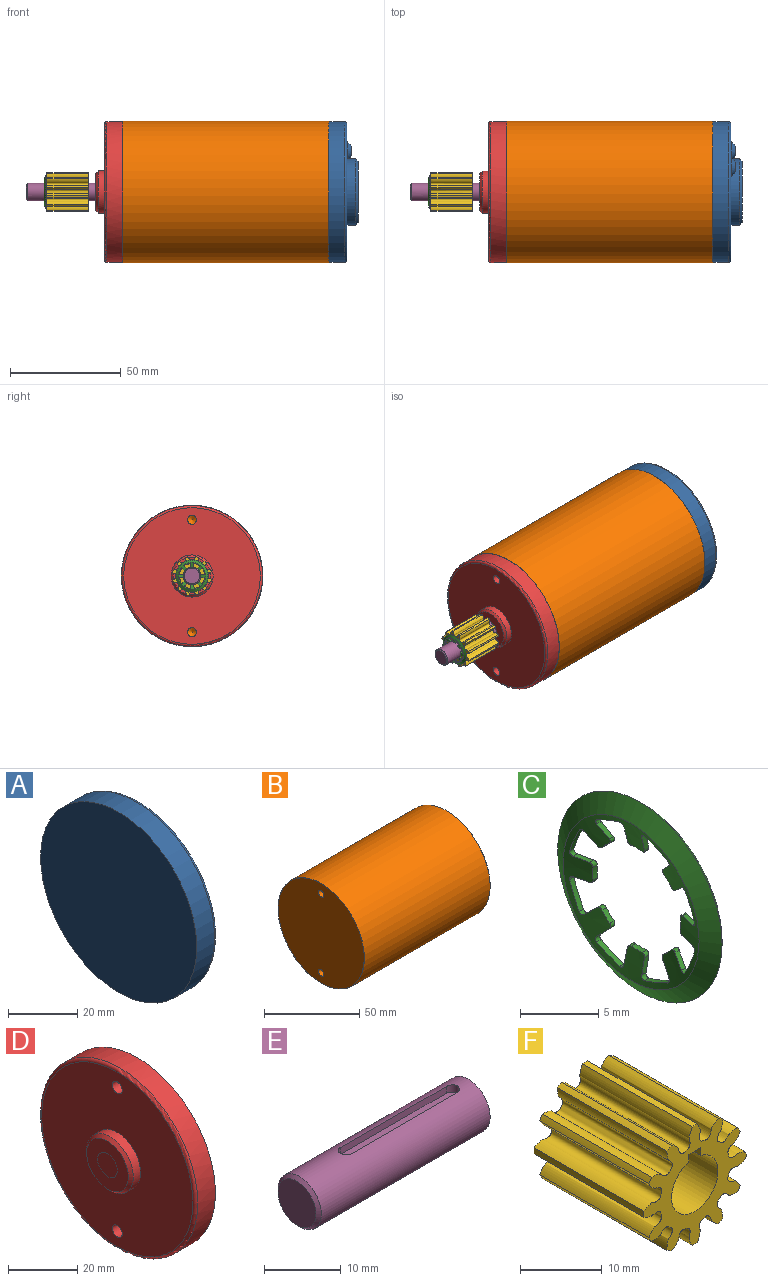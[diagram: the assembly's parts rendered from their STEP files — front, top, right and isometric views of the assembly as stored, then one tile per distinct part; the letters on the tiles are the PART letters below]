
ASSEMBLY  parts=6 mates=5
PART A: 13 faces, bbox 13.2x69x69 mm
  f0: plane 4.24x4.24mm, normal (1,0,0), area 14.1mm2, adj f3
  f1: plane 28.04x28.04mm, normal (1,0,0), area 617.6mm2, adj f4
  f2: plane 4.24x4.24mm, normal (1,0,0), area 14.1mm2, adj f5
  f3: cone r=2.12mm half-angle=45deg, axis (-1,0,0), area 62.9mm2, adj f0,f6
  f4: cone r=14.02mm half-angle=45deg, axis (-1,0,0), area 131.2mm2, adj f1,f7
  f5: cone r=2.12mm half-angle=45deg, axis (-1,0,0), area 62.9mm2, adj f2,f8
  f6: cylinder r=4.32mm len=8.64mm, axis (-1,0,0), area 1.3mm2, adj f3,f9
  f7: cylinder r=15.04mm len=30.07mm, axis (1,0,0), area 376.4mm2, adj f4,f9
  f8: cylinder r=4.32mm len=8.64mm, axis (-1,0,0), area 1.3mm2, adj f5,f9
  f9: plane 61.75x61.75mm, normal (1,0,0), area 2167.7mm2, adj f6,f7,f8,f10
  f10: torus R=30.88mm, axis (1,0,0), area 311mm2, adj f9,f11
  f11: cylinder r=31.88mm len=63.75mm, axis (1,0,0), area 1448mm2, adj f10,f12
  f12: plane 63.75x63.75mm, normal (-1,0,0), area 3192.3mm2, adj f11
PART B: 9 faces, bbox 93.1x64x64 mm
  f0: plane 63.75x63.75mm, normal (1,0,0), area 3192.3mm2, adj f1
  f1: plane 64.01x64.01mm, normal (1,0,0), area 25.5mm2, adj f0,f2
  f2: cylinder r=32mm len=93.14mm, axis (1,0,0), area 18729.4mm2, adj f1,f3
  f3: plane 64.01x64.01mm, normal (-1,0,0), area 25.5mm2, adj f2,f4
  f4: plane 63.75x63.75mm, normal (-1,0,0), area 3166.7mm2, adj f3,f6,f8
  f5: cone r=2.02mm half-angle=59deg, axis (-1,0,0), area 14.9mm2, adj f6
  f6: cylinder r=2.02mm len=5.38mm, axis (-1,0,0), area 68.3mm2, adj f4,f5
  f7: cone r=2.02mm half-angle=59deg, axis (-1,0,0), area 14.9mm2, adj f8
  f8: cylinder r=2.02mm len=5.38mm, axis (-1,0,0), area 68.3mm2, adj f4,f7
PART C: 69 faces, bbox 1.1x14.9x14.9 mm
  f0: cylinder r=0.25mm len=0.46mm, axis (-1,0,0), area 0.2mm2, adj f11,f12,f14,f63
  f1: cylinder r=0.25mm len=0.46mm, axis (-1,0,0), area 0.2mm2, adj f11,f12,f56,f62
  f2: cylinder r=0.25mm len=0.46mm, axis (-1,0,0), area 0.2mm2, adj f11,f12,f49,f55
  f3: cylinder r=0.25mm len=0.46mm, axis (-1,0,0), area 0.2mm2, adj f11,f12,f42,f48
  f4: cylinder r=0.25mm len=0.46mm, axis (-1,0,0), area 0.2mm2, adj f11,f12,f35,f41
  f5: cylinder r=0.25mm len=0.46mm, axis (-1,0,0), area 0.2mm2, adj f11,f12,f28,f34
  f6: cylinder r=0.25mm len=0.46mm, axis (-1,0,0), area 0.2mm2, adj f11,f12,f21,f27
  f7: cylinder r=0.25mm len=0.46mm, axis (-1,0,0), area 0.2mm2, adj f11,f12,f13,f17
  f8: cone r=7.42mm half-angle=58.1deg, axis (1,0,0), area 64.3mm2, adj f9,f12
  f9: cone r=7.15mm half-angle=45deg, axis (-1,0,0), area 17.4mm2, adj f8,f10
  f10: cone r=6.08mm half-angle=58.1deg, axis (1,0,0), area 52.2mm2, adj f9,f11
  f11: cone r=4.66mm half-angle=76.9deg, axis (-1,0,0), area 36.8mm2, adj f0,f1,f2,f3,f4,f5,f6,f7
  f12: cone r=4.66mm half-angle=76.9deg, axis (-1,0,0), area 38.9mm2, adj f0,f1,f2,f3,f4,f5,f6,f7
  f13: cylinder r=3.97mm len=0.99mm, axis (-1,0,0), area 0.4mm2, adj f7,f11,f12,f26
  f14: cylinder r=3.97mm len=0.7mm, axis (-1,0,0), area 0.4mm2, adj f0,f11,f12,f20
  f15: plane 0.89x0.86mm, normal (0,0.69,0.72), area 0.5mm2, adj f11,f12,f18,f20
  f16: cylinder r=11.39mm len=2.06mm, axis (-1,0,0), area 0.9mm2, adj f11,f12,f18,f19
  f17: plane 1.23x0.69mm, normal (0,-0.02,-1), area 0.5mm2, adj f7,f11,f12,f19
  f18: cylinder r=0.25mm len=0.46mm, axis (-1,0,0), area 0.2mm2, adj f11,f12,f15,f16
  f19: cylinder r=0.25mm len=0.46mm, axis (-1,0,0), area 0.2mm2, adj f11,f12,f16,f17
  f20: cylinder r=0.25mm len=0.46mm, axis (-1,0,0), area 0.2mm2, adj f11,f12,f14,f15
  f21: plane 0.89x0.86mm, normal (0,0.69,-0.72), area 0.5mm2, adj f6,f11,f12,f22
  f22: cylinder r=0.25mm len=0.46mm, axis (-1,0,0), area 0.2mm2, adj f11,f12,f21,f23
  f23: cylinder r=11.39mm len=2.06mm, axis (-1,0,0), area 0.9mm2, adj f11,f12,f22,f24
  f24: cylinder r=0.25mm len=0.46mm, axis (-1,0,0), area 0.2mm2, adj f11,f12,f23,f25
  f25: plane 1.23x0.69mm, normal (0,-0.02,1), area 0.5mm2, adj f11,f12,f24,f26
  f26: cylinder r=0.25mm len=0.46mm, axis (-1,0,0), area 0.2mm2, adj f11,f12,f13,f25
  f27: cylinder r=3.97mm len=0.7mm, axis (-1,0,0), area 0.4mm2, adj f6,f11,f12,f33
  f28: plane 1.23x0.69mm, normal (0,1,-0.02), area 0.5mm2, adj f5,f11,f12,f29
  f29: cylinder r=0.25mm len=0.46mm, axis (-1,0,0), area 0.2mm2, adj f11,f12,f28,f30
  f30: cylinder r=11.39mm len=2.06mm, axis (-1,0,0), area 0.9mm2, adj f11,f12,f29,f31
  f31: cylinder r=0.25mm len=0.46mm, axis (-1,0,0), area 0.2mm2, adj f11,f12,f30,f32
  f32: plane 0.89x0.86mm, normal (0,-0.72,0.69), area 0.5mm2, adj f11,f12,f31,f33
  f33: cylinder r=0.25mm len=0.46mm, axis (-1,0,0), area 0.2mm2, adj f11,f12,f27,f32
  f34: cylinder r=3.97mm len=0.99mm, axis (-1,0,0), area 0.4mm2, adj f5,f11,f12,f40
  f35: plane 0.89x0.86mm, normal (0,0.72,0.69), area 0.5mm2, adj f4,f11,f12,f36
  f36: cylinder r=0.25mm len=0.46mm, axis (-1,0,0), area 0.2mm2, adj f11,f12,f35,f37
  f37: cylinder r=11.39mm len=2.06mm, axis (-1,0,0), area 0.9mm2, adj f11,f12,f36,f38
  f38: cylinder r=0.25mm len=0.46mm, axis (-1,0,0), area 0.2mm2, adj f11,f12,f37,f39
  f39: plane 1.23x0.69mm, normal (0,-1,-0.02), area 0.5mm2, adj f11,f12,f38,f40
  f40: cylinder r=0.25mm len=0.46mm, axis (-1,0,0), area 0.2mm2, adj f11,f12,f34,f39
  f41: cylinder r=3.97mm len=0.7mm, axis (-1,0,0), area 0.4mm2, adj f4,f11,f12,f47
  f42: plane 1.23x0.69mm, normal (0,0.02,1), area 0.5mm2, adj f3,f11,f12,f43
  f43: cylinder r=0.25mm len=0.46mm, axis (-1,0,0), area 0.2mm2, adj f11,f12,f42,f44
  f44: cylinder r=11.39mm len=2.06mm, axis (-1,0,0), area 0.9mm2, adj f11,f12,f43,f45
  f45: cylinder r=0.25mm len=0.46mm, axis (-1,0,0), area 0.2mm2, adj f11,f12,f44,f46
  f46: plane 0.89x0.86mm, normal (0,-0.69,-0.72), area 0.5mm2, adj f11,f12,f45,f47
  f47: cylinder r=0.25mm len=0.46mm, axis (-1,0,0), area 0.2mm2, adj f11,f12,f41,f46
  f48: cylinder r=3.97mm len=0.99mm, axis (-1,0,0), area 0.4mm2, adj f3,f11,f12,f54
  f49: plane 0.89x0.86mm, normal (0,-0.69,0.72), area 0.5mm2, adj f2,f11,f12,f50
  f50: cylinder r=0.25mm len=0.46mm, axis (-1,0,0), area 0.2mm2, adj f11,f12,f49,f51
  f51: cylinder r=11.39mm len=2.06mm, axis (-1,0,0), area 0.9mm2, adj f11,f12,f50,f52
  f52: cylinder r=0.25mm len=0.46mm, axis (-1,0,0), area 0.2mm2, adj f11,f12,f51,f53
  f53: plane 1.23x0.69mm, normal (0,0.02,-1), area 0.5mm2, adj f11,f12,f52,f54
  f54: cylinder r=0.25mm len=0.46mm, axis (-1,0,0), area 0.2mm2, adj f11,f12,f48,f53
  f55: cylinder r=3.97mm len=0.7mm, axis (-1,0,0), area 0.4mm2, adj f2,f11,f12,f61
  f56: plane 1.23x0.69mm, normal (0,-1,0.02), area 0.5mm2, adj f1,f11,f12,f57
  f57: cylinder r=0.25mm len=0.46mm, axis (-1,0,0), area 0.2mm2, adj f11,f12,f56,f58
  f58: cylinder r=11.39mm len=2.06mm, axis (-1,0,0), area 0.9mm2, adj f11,f12,f57,f59
  f59: cylinder r=0.25mm len=0.46mm, axis (-1,0,0), area 0.2mm2, adj f11,f12,f58,f60
  f60: plane 0.89x0.86mm, normal (0,0.72,-0.69), area 0.5mm2, adj f11,f12,f59,f61
  f61: cylinder r=0.25mm len=0.46mm, axis (-1,0,0), area 0.2mm2, adj f11,f12,f55,f60
  f62: cylinder r=3.97mm len=0.99mm, axis (-1,0,0), area 0.4mm2, adj f1,f11,f12,f68
  f63: plane 0.89x0.86mm, normal (0,-0.72,-0.69), area 0.5mm2, adj f0,f11,f12,f64
  f64: cylinder r=0.25mm len=0.46mm, axis (-1,0,0), area 0.2mm2, adj f11,f12,f63,f65
  f65: cylinder r=11.39mm len=2.06mm, axis (-1,0,0), area 0.9mm2, adj f11,f12,f64,f66
  f66: cylinder r=0.25mm len=0.46mm, axis (-1,0,0), area 0.2mm2, adj f11,f12,f65,f67
  f67: plane 1.23x0.69mm, normal (0,1,0.02), area 0.5mm2, adj f11,f12,f66,f68
  f68: cylinder r=0.25mm len=0.46mm, axis (-1,0,0), area 0.2mm2, adj f11,f12,f62,f67
PART D: 10 faces, bbox 12.2x69x69 mm
  f0: cone r=9.53mm half-angle=45deg, axis (1,0,0), area 81.4mm2, adj f4,f7
  f1: cylinder r=2.02mm len=8.23mm, axis (-1,0,0), area 104.4mm2, adj f6,f9
  f2: cylinder r=2.02mm len=8.23mm, axis (-1,0,0), area 104.4mm2, adj f6,f9
  f3: torus R=30.88mm, axis (-1,0,0), area 311mm2, adj f5,f6
  f4: cylinder r=9.53mm len=19.05mm, axis (1,0,0), area 178.6mm2, adj f0,f6
  f5: cylinder r=31.88mm len=63.75mm, axis (1,0,0), area 1448mm2, adj f3,f9
  f6: plane 61.75x61.75mm, normal (-1,0,0), area 2684.5mm2, adj f1,f2,f3,f4
  f7: plane 17.02x17.02mm, normal (-1,0,0), area 177.2mm2, adj f0,f8
  f8: plane 8x8mm, normal (-1,0,0), area 50.3mm2, adj f7
  f9: plane 63.75x63.75mm, normal (1,0,0), area 3166.7mm2, adj f1,f2,f5
PART E: 9 faces, bbox 31.6x8x8 mm
  f0: plane 21.5x2mm, normal (0,0,1), area 42.1mm2, adj f2,f3,f4,f5
  f1: plane 7x7mm, normal (-1,0,0), area 38.5mm2, adj f6
  f2: plane 19.5x1.07mm, normal (0,1,0), area 20.9mm2, adj f0,f3,f5,f7
  f3: cylinder r=1mm len=2mm, axis (0,0,1), area 3.4mm2, adj f0,f2,f4,f7
  f4: plane 19.5x1.07mm, normal (0,-1,0), area 20.9mm2, adj f0,f3,f5,f7
  f5: cylinder r=1mm len=2mm, axis (0,0,-1), area 3.4mm2, adj f0,f2,f4,f7
  f6: cone r=4mm half-angle=45deg, axis (1,0,0), area 16.7mm2, adj f1,f7
  f7: cylinder r=4mm len=31.1mm, axis (1,0,0), area 739mm2, adj f2,f3,f4,f5,f6,f8
  f8: plane 8x8mm, normal (1,0,0), area 50.3mm2, adj f7
PART F: 30 faces, bbox 18x19.2x18 mm
  f0: cylinder r=4.03mm len=19mm, axis (0,1,0), area 441.1mm2, adj f2,f26,f27,f28
  f1: cylinder r=8.89mm len=19mm, axis (0,-1,0), area 17.2mm2, adj f2,f14,f15,f26
  f2: plane 17.95x17.95mm, normal (0,-1,0), area 120.6mm2, adj f0,f1,f3,f4,f5,f6,f7,f8
  f3: cylinder r=8.89mm len=19mm, axis (0,-1,0), area 17.2mm2, adj f2,f24,f25,f26
  f4: cylinder r=8.89mm len=19mm, axis (0,-1,0), area 17.2mm2, adj f2,f14,f25,f26
  f5: cylinder r=8.89mm len=19mm, axis (0,-1,0), area 17.2mm2, adj f2,f23,f24,f26
  f6: cylinder r=8.89mm len=19mm, axis (0,-1,0), area 17.2mm2, adj f2,f22,f23,f26
  f7: cylinder r=8.89mm len=19mm, axis (0,-1,0), area 17.2mm2, adj f2,f21,f22,f26
  f8: cylinder r=8.89mm len=19mm, axis (0,-1,0), area 17.2mm2, adj f2,f20,f21,f26
  f9: cylinder r=8.89mm len=19mm, axis (0,-1,0), area 17.2mm2, adj f2,f19,f20,f26
  f10: cylinder r=8.89mm len=19mm, axis (0,-1,0), area 17.2mm2, adj f2,f18,f19,f26
  f11: cylinder r=8.89mm len=19mm, axis (0,-1,0), area 17.2mm2, adj f2,f17,f18,f26
  f12: cylinder r=8.89mm len=19mm, axis (0,-1,0), area 17.2mm2, adj f2,f16,f17,f26
  f13: cylinder r=8.89mm len=19mm, axis (0,-1,0), area 17.2mm2, adj f2,f15,f16,f26
  f14: bspline ~19x3.59mm, area 136.3mm2, adj f1,f2,f4,f26
  f15: bspline ~19x3.59mm, area 136.3mm2, adj f1,f2,f13,f26
  f16: bspline ~19x3.56mm, area 136.3mm2, adj f2,f12,f13,f26
  f17: bspline ~19x3.59mm, area 136.3mm2, adj f2,f11,f12,f26
  f18: bspline ~19x3.59mm, area 136.3mm2, adj f2,f10,f11,f26
  f19: bspline ~19x3.56mm, area 136.3mm2, adj f2,f9,f10,f26
  f20: bspline ~19x3.59mm, area 136.3mm2, adj f2,f8,f9,f26
  f21: bspline ~19x3.59mm, area 136.3mm2, adj f2,f7,f8,f26
  f22: bspline ~19x3.56mm, area 136.3mm2, adj f2,f6,f7,f26
  f23: bspline ~19x3.59mm, area 136.3mm2, adj f2,f5,f6,f26
  f24: bspline ~19x3.59mm, area 136.3mm2, adj f2,f3,f5,f26
  f25: bspline ~19x3.56mm, area 136.3mm2, adj f2,f3,f4,f26
  f26: plane 17.95x17.95mm, normal (0,1,0), area 118.5mm2, adj f0,f1,f3,f4,f5,f6,f7,f8
  f27: plane 19x1.13mm, normal (1,0,0), area 21.5mm2, adj f0,f2,f26,f29
  f28: plane 19x1.13mm, normal (-1,0,0), area 21.5mm2, adj f0,f2,f26,f29
  f29: plane 19x2.05mm, normal (0,0,-1), area 39mm2, adj f2,f26,f27,f28
PLACE A t=(-54.8,0,0)mm
PLACE B t=(-54.8,0,0)mm
PLACE C rot(axis=(1,0,0),179.1deg) t=(-82.25,0,0)mm
PLACE D t=(-54.8,0,0)mm
PLACE E rot(axis=(-1,0,0),135.9deg) t=(-54.8,0,0)mm
PLACE F rot(axis=(-0.68,-0.68,-0.28),149.2deg) t=(-71.47,0,0)mm
MATE fastened D.f0 <-> B.f2  axis (1,0,0) through (-46.57,0,0)mm
MATE revolute A.f4 <-> E.f6  axis (-1,0,0) through (-58.8,0,0)mm
MATE fastened F.f0 <-> E.f6  axis (1,0,0) through (-61.98,0,0)mm
MATE fastened C.f27 <-> F.f0  axis (1,0,0) through (-81.36,0,0)mm
MATE fastened B.f2 <-> A.f4  axis (1,0,0) through (46.57,0,0)mm
